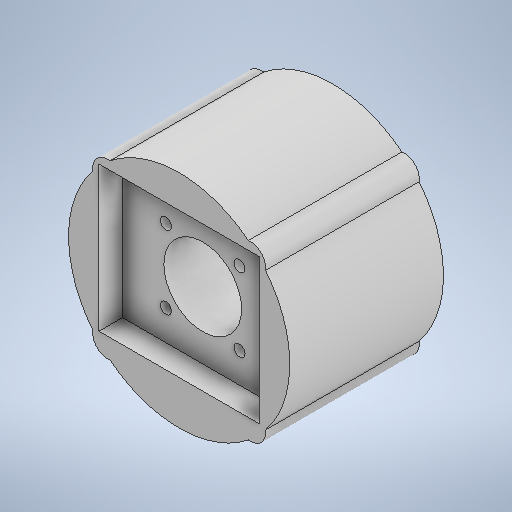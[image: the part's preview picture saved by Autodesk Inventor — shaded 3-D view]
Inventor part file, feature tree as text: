
AUTODESK INVENTOR PART (.ipt)
format: ipt  version: 2025.1 (Build 291241000, 241)  size: 329,728 bytes
history: native  units: mm
features: sketch x6, extrude x5
ambient origin geometry x8: Origin, YZ Plane, XZ Plane, XY Plane, X Axis, Y Axis, Z Axis, Center Point
bodies: Solid1 (feature_tree)
feature tree (11):
  extrude  "Extrusion1"  Depth=10.0mm
  extrude  "Extrusion6"  Depth=70.05mm
  extrude  "Extrusion7"  Depth=74.060786mm
  extrude  "Extrusion8"  Depth=48.3mm TaperAngle=0.0deg
  extrude  "Extrusion9"  TaperAngle=0.0deg  [1 undecoded]
  sketch  "Sketch1"  dims[d0=10.0mm d1=0.25mm]
  sketch  "Skizze - Runde Anordnung1"  dims[d2=40.0mm d4=360.0deg d6=70.05mm]
  sketch  "Skizze6"  dims[d7=0.25mm d8=74.060786mm]
  sketch  "Skizze7"  dims[d9=73.5mm d10=48.3mm d11=0.0mm]
  sketch  "Skizze8"  dims[d33=24.45mm d34=0.0mm d35=0.0mm]
  sketch  "Skizze9"  dims[d38=7.4mm d39=0.0mm d40=23.14mm d41=23.14mm d42=3.5mm d43=3.5mm d44=3.5mm d45=3.5mm d46=0.0mm d47=0.0mm d48=1.75mm d49=50.46mm d50=45.54mm d51=6.2mm d52=6.2mm d53=6.2mm d54=6.2mm d55=3.5mm d56=0.0mm d30=0.5mm d31=0.872665mm d32=0.5mm]
note: 1 required parameter value undecoded (feature->parameter linkage not recoverable at this tier; creation-order binding heuristic only, values carry confidence <= 0.55)
